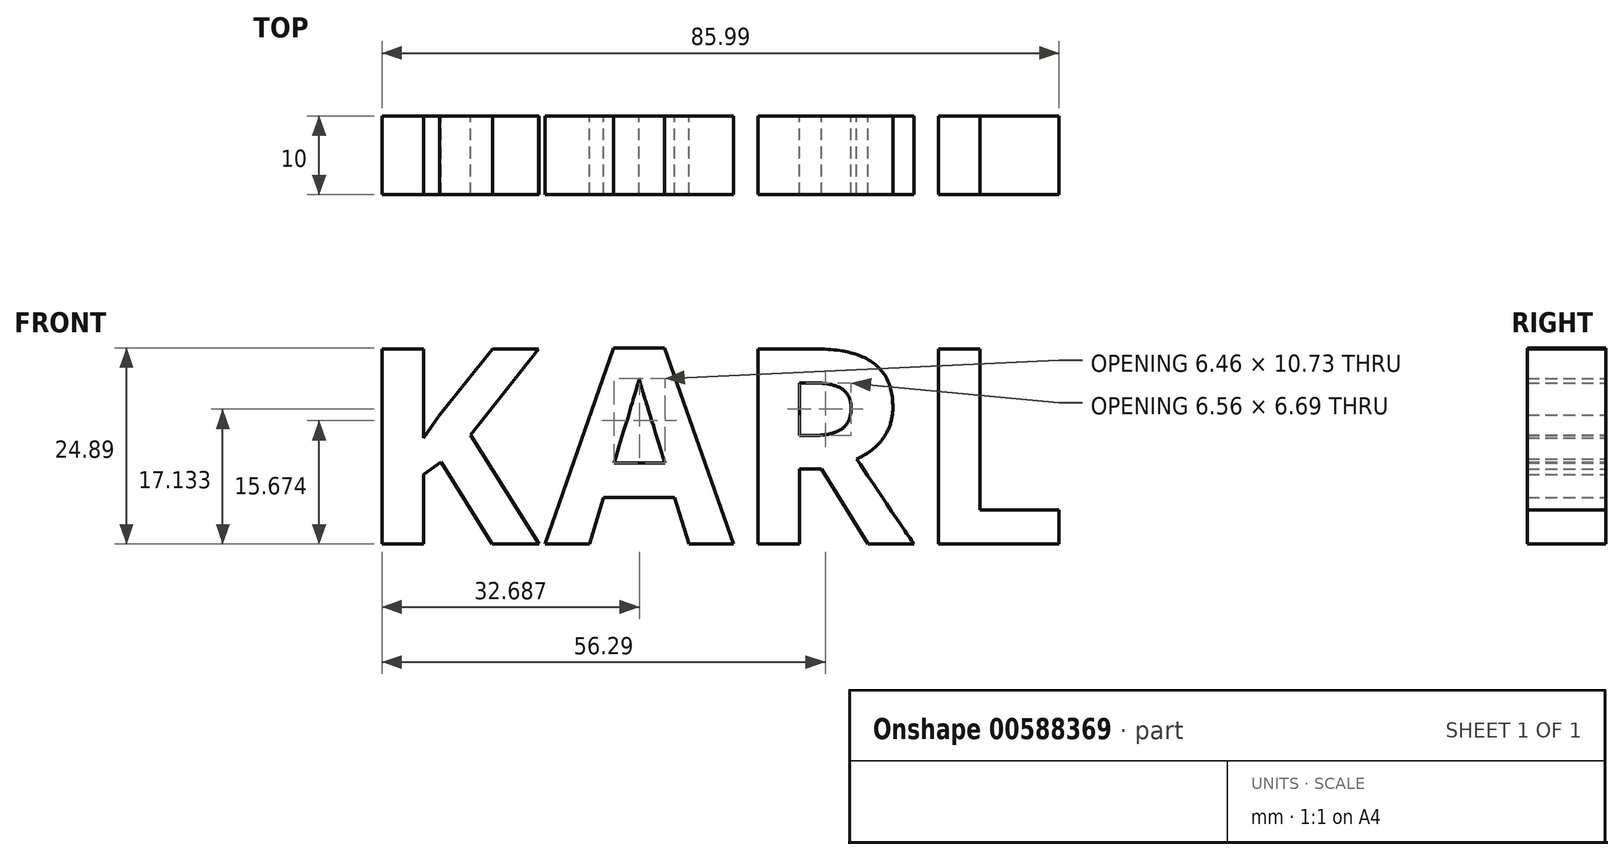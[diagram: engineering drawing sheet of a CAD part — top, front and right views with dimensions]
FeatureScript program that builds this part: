
annotation { "Feature Type Name" : "Feature", "Feature Type Description" : "" }
export const myFeature = defineFeature(function(context is Context, id is Id, definition is map)
    precondition{}
    {
        {
            var Q0;
            Q0=qCreatedBy(makeId("Front.planeOp"),FACE);
            var sketch = newSketch(context, id + "F0", { "sketchPlane" : qUnion([Q0])});
            skText(sketch, "E0", { "text": "KARL", "fontName": "OpenSans-Bold.ttf"});
            const initialGuessF0  = {"E0": [-0.07134, 0, 1, 0, 0.025]};
            skSetInitialGuess(sketch, initialGuessF0);
            skSolve(sketch);
        }
        {
            var Q0;
            Q0=qSketchRegion(id+"F0",true);
            extrude(context, id + "F1", {"entities" : qUnion([Q0]), "depth" : 10 * mm, "offsetDistance" : 25 * mm});
        }
    });
